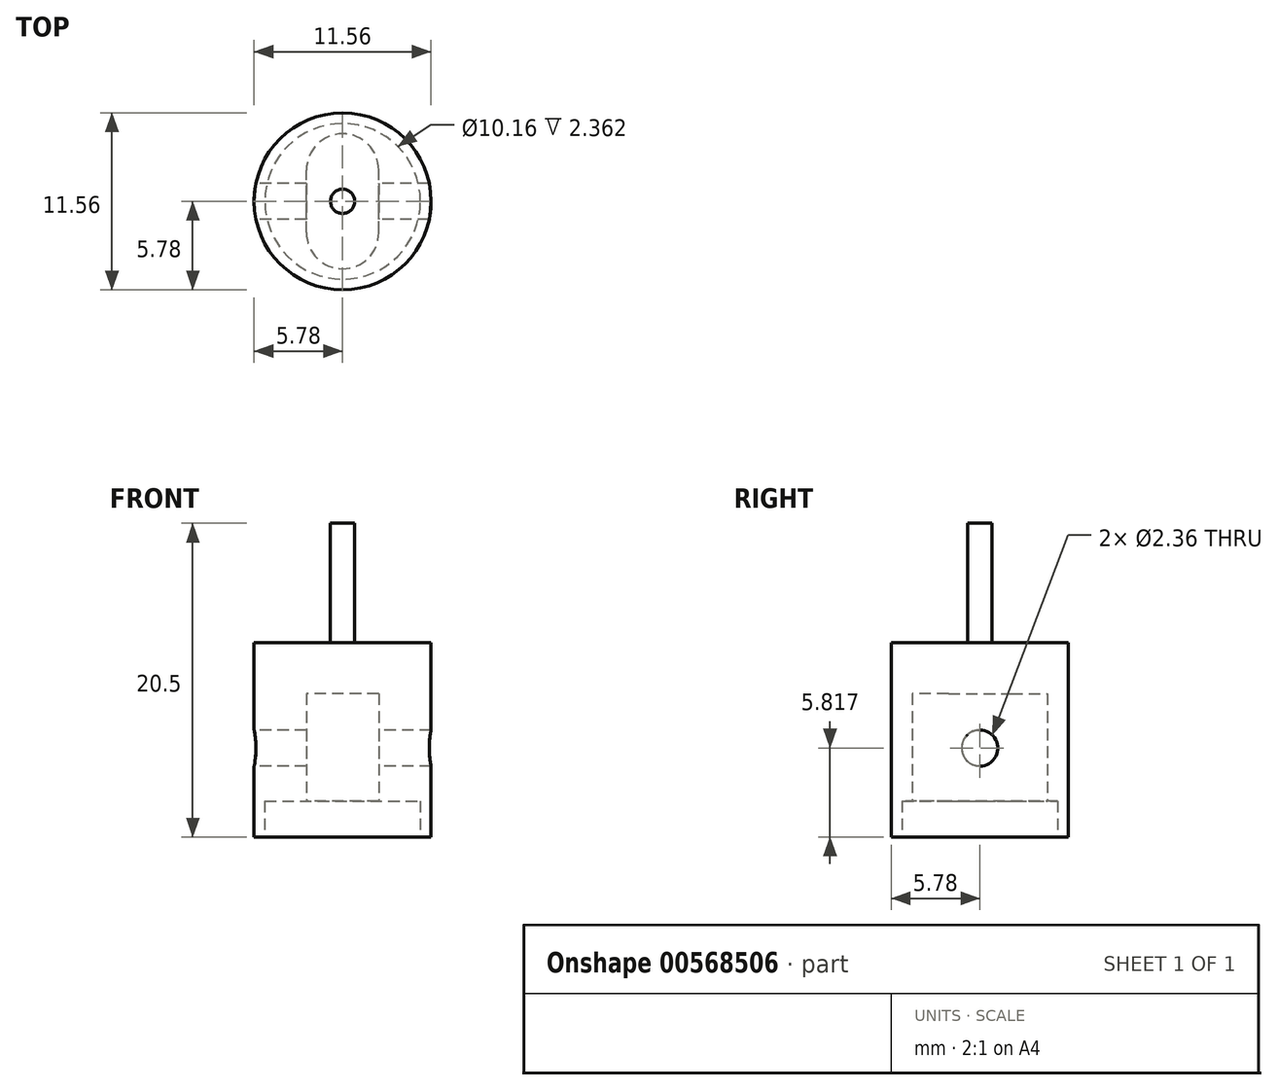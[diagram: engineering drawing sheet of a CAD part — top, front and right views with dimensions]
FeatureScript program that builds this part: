
annotation { "Feature Type Name" : "Feature", "Feature Type Description" : "" }
export const myFeature = defineFeature(function(context is Context, id is Id, definition is map)
    precondition{}
    {
        {
            var Q0;
            Q0=qCreatedBy(makeId("Top.planeOp"),FACE);
            var sketch = newSketch(context, id + "F0", { "sketchPlane" : qUnion([Q0])});
            skCircle(sketch, "E0", {"center": v(0, 0) * mm, "radius": 5.78 * mm});
            skSolve(sketch);
        }
        {
            var Q0;
            Q0 = qSketchRegion(id + "F0", true);
            extrude(context, id + "F1", {"entities" : qUnion([Q0]), "depth" : 12.7 * mm, "offsetDistance" : 25.4 * mm});
        }
        {
            var Q0;
            Q0=makeQuery(id+"F1.opExtrude","CAP_FACE",FACE,{"disambiguationData":[OSD([sQuery(id+"F0.wireOp",EDGE,"E0")])],"isStart":true});
            var sketch = newSketch(context, id + "F2", { "sketchPlane" : qUnion([Q0])});
            skCircle(sketch, "E1", {"center": v(0, 0) * mm, "radius": 5.08 * mm});
            skSolve(sketch);
        }
        {
            var Q0;
            Q0 = qSketchRegion(id + "F2", true);
            extrude(context, id + "F3", {"entities" : qUnion([Q0]), "operationType" : NewBodyOperationType.REMOVE, "oppositeDirection" : true, "depth" : 2.36 * mm, "offsetDistance" : 25.4 * mm});
        }
        {
            var Q0;
            Q0=makeQuery(id+"F3.boolean.opBoolean","COPY",FACE,{"derivedFrom":makeQuery(id+"F3.opExtrude","CAP_FACE",FACE,{"disambiguationData":[OSD([sQuery(id+"F2.wireOp",EDGE,"E1")])],"isStart":false})});
            var sketch = newSketch(context, id + "F4", { "sketchPlane" : qUnion([Q0])});
            skPoint(sketch, "E2", {"position": v(0, 4.4) * mm});
            skPoint(sketch, "E3", {"position": v(0, -4.4) * mm});
            skLineSegment(sketch, "E4", {"start": v(2.36, 3.22) * mm, "end": v(2.36, -3.39) * mm});
            skLineSegment(sketch, "E5", {"start": v(-2.36, 3.03) * mm, "end": v(-2.36, -3) * mm});
            skLineSegment(sketch, "E6", {"start": v(0, 4.4) * mm, "end": v(0, 2.04) * mm});
            skArc(sketch, "E7", {"start": v(2.36, 2.04) * mm, "mid": v(0, 4.4) * mm, "end": v(-2.36, 2.04) * mm});
            skLineSegment(sketch, "E8", {"start": v(0, -4.4) * mm, "end": v(0, -2.04) * mm});
            skArc(sketch, "E9", {"start": v(-2.36, -2.04) * mm, "mid": v(0, -4.4) * mm, "end": v(2.36, -2.04) * mm});
            skSolve(sketch);
        }
        {
            var Q0;
            Q0 = qSketchRegion(id + "F4", true);
            extrude(context, id + "F5", {"entities" : qUnion([Q0]), "operationType" : NewBodyOperationType.REMOVE, "oppositeDirection" : true, "depth" : 7 * mm, "offsetDistance" : 25.4 * mm});
        }
        {
            var Q0;
            Q0=qCreatedBy(makeId("Right.planeOp"),FACE);
            var sketch = newSketch(context, id + "F6", { "sketchPlane" : qUnion([Q0])});
            skLineSegment(sketch, "E10", {"start": v(0, 0) * mm, "end": v(0, 5.82) * mm});
            skCircle(sketch, "E11", {"center": v(0, 5.82) * mm, "radius": 1.18 * mm});
            skSolve(sketch);
        }
        {
            var Q0;
            Q0 = qSketchRegion(id + "F6", true);
            extrude(context, id + "F7", {"entities" : qUnion([Q0]), "operationType" : NewBodyOperationType.REMOVE, "endBound" : BoundingType.SYMMETRIC, "depth" : 25.4 * mm, "offsetDistance" : 25.4 * mm});
        }
        {
            var Q0;
            Q0=makeQuery(id+"F1.opExtrude","CAP_FACE",FACE,{"disambiguationData":[OSD([sQuery(id+"F0.wireOp",EDGE,"E0")])],"isStart":false});
            var sketch = newSketch(context, id + "F8", { "sketchPlane" : qUnion([Q0])});
            skCircle(sketch, "E12", {"center": v(0, 0) * mm, "radius": 0.8 * mm});
            skSolve(sketch);
        }
        {
            var Q0;
            Q0 = qSketchRegion(id + "F8", true);
            extrude(context, id + "F9", {"entities" : qUnion([Q0]), "operationType" : NewBodyOperationType.ADD, "depth" : 7.8 * mm, "offsetDistance" : 25.4 * mm});
        }
    });
